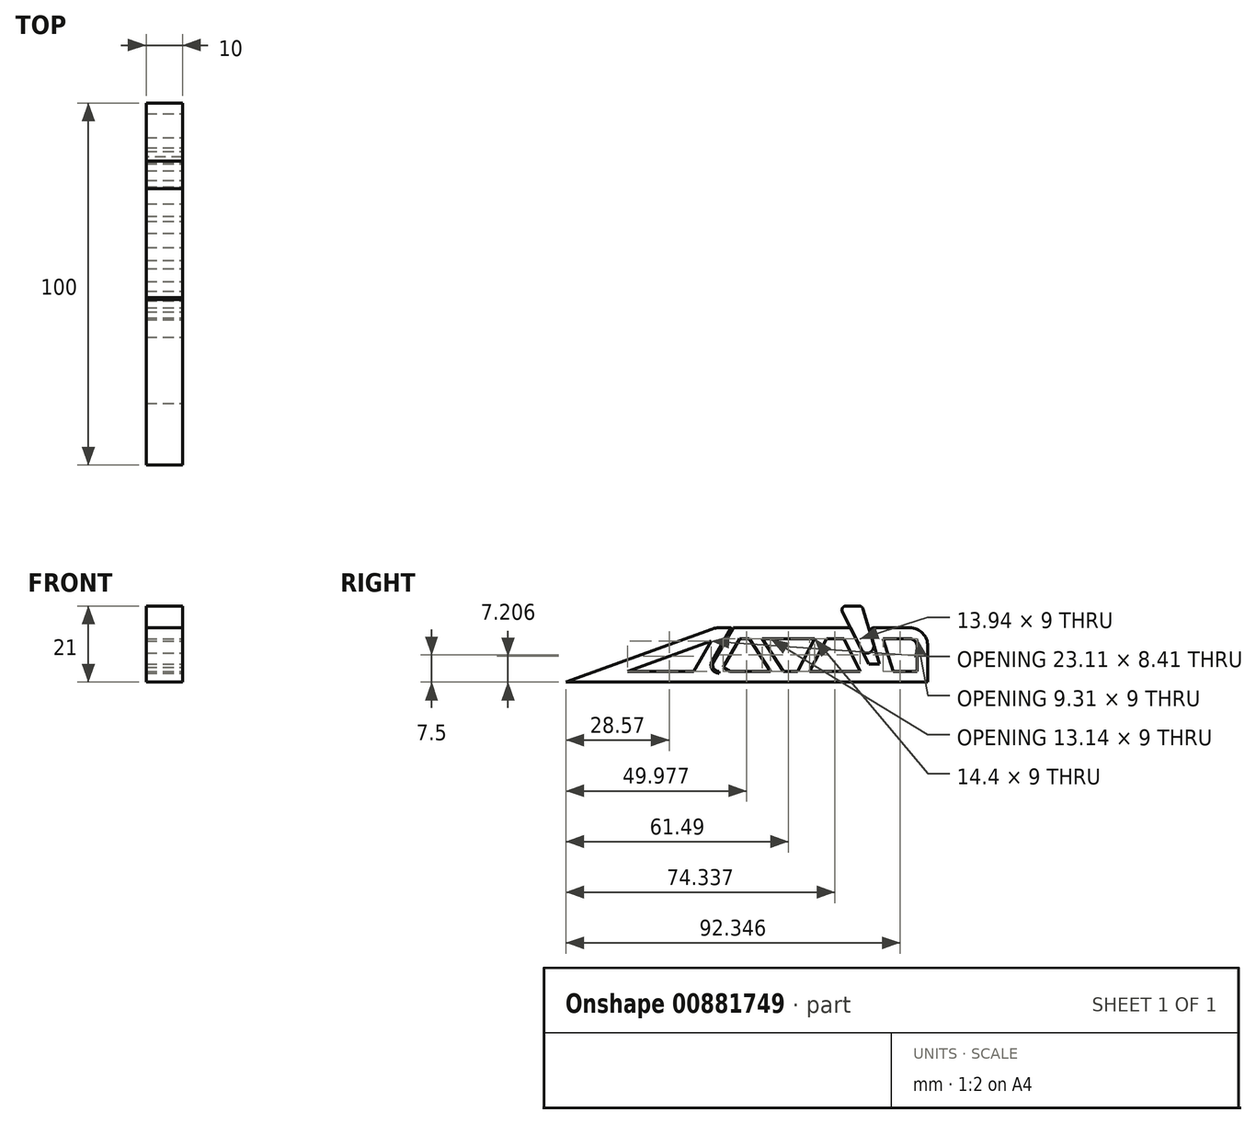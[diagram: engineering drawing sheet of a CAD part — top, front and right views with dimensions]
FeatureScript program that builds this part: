
annotation { "Feature Type Name" : "Feature", "Feature Type Description" : "" }
export const myFeature = defineFeature(function(context is Context, id is Id, definition is map)
    precondition{}
    {
        {
            var Q0;
            Q0=qCreatedBy(makeId("Right.planeOp"),FACE);
            var sketch = newSketch(context, id + "F0", { "sketchPlane" : qUnion([Q0])});
            skLineSegment(sketch, "E0", {"start": v(-50, 0) * mm, "end": v(50, 0) * mm});
            skLineSegment(sketch, "E1", {"start": v(-50, 0) * mm, "end": v(-8.79, 15) * mm});
            skLineSegment(sketch, "E2", {"start": v(50, 0) * mm, "end": v(50, 15) * mm});
            skLineSegment(sketch, "E3", {"start": v(-8.79, 15) * mm, "end": v(50, 15) * mm});
            skSolve(sketch);
        }
        {
            var Q0;
            Q0=qSketchRegion(id+"F0",true);
            extrude(context, id + "F1", {"entities" : qUnion([Q0]), "endBound" : BoundingType.SYMMETRIC, "depth" : 10 * mm, "offsetDistance" : 25 * mm});
        }
        {
            var Q0;
            Q0=makeQuery(id+"F1.opExtrude","SWEPT_EDGE",EDGE,{"disambiguationData":[OSD([sQuery(id+"F0.wireOp",EDGE,"E2"),sQuery(id+"F0.wireOp",EDGE,"E3")])]});
            var Q1;
            Q1=makeQuery(id+"F1.opExtrude","SWEPT_EDGE",EDGE,{"disambiguationData":[OSD([sQuery(id+"F0.wireOp",EDGE,"E1"),sQuery(id+"F0.wireOp",EDGE,"E3")])]});
            var Q2;
            Q2=makeQuery(id+"FClCLpVwUMpyTBV_1.opFillet","BLEND_EDGE",EDGE,{"blendedFrom":[makeQuery(id+"F1.opExtrude","SWEPT_EDGE",EDGE,{"disambiguationData":[OSD([sQuery(id+"F0.wireOp",EDGE,"E0"),sQuery(id+"F0.wireOp",EDGE,"E2")])]}),makeQuery(id+"F1.opExtrude","SWEPT_FACE",FACE,{"disambiguationData":[OSD([sQuery(id+"F0.wireOp",EDGE,"E3")])]})],"blendedInto":[makeQuery(id+"F1.opExtrude","SWEPT_FACE",FACE,{"disambiguationData":[OSD([sQuery(id+"F0.wireOp",EDGE,"E3")])]})]});
            fillet(context, id + "F2", {"entities" : qUnion([Q0, Q1, Q2]), "radius" : 5 * mm, "tangentPropagation" : true, "allowEdgeOverflow" : false});
        }
        {
            var Q0;
            Q0=makeQuery(id+"F1.opExtrude","CAP_FACE",FACE,{"disambiguationData":[OSD([sQuery(id+"F0.wireOp",EDGE,"E0"),sQuery(id+"F0.wireOp",EDGE,"E1"),sQuery(id+"F0.wireOp",EDGE,"E2"),sQuery(id+"F0.wireOp",EDGE,"E3")])],"isStart":false});
            var sketch = newSketch(context, id + "F3", { "sketchPlane" : qUnion([Q0])});
            skLineSegment(sketch, "E4", {"start": v(-4.34, 15) * mm, "end": v(-9.62, 5.85) * mm});
            skArc(sketch, "E5", {"start": v(-9.62, 5.85) * mm, "mid": v(-9.62, 3.61) * mm, "end": v(-7.68, 2.5) * mm});
            skLineSegment(sketch, "E6.0", {"start": v(-3.76, 15) * mm, "end": v(-9.2, 5.6) * mm});
            skArc(sketch, "E7.0", {"start": v(-9.2, 5.6) * mm, "mid": v(-9.19, 3.86) * mm, "end": v(-7.68, 3) * mm});
            skLineSegment(sketch, "E8", {"start": v(-4.34, 15) * mm, "end": v(-3.76, 15) * mm});
            skLineSegment(sketch, "E9", {"start": v(-7.68, 3) * mm, "end": v(-7.68, 2.5) * mm});
            skLineSegment(sketch, "E10", {"start": v(28.66, 15) * mm, "end": v(33.66, 5) * mm});
            skLineSegment(sketch, "E11", {"start": v(33.66, 15) * mm, "end": v(36.66, 5) * mm});
            skLineSegment(sketch, "E12", {"start": v(33.66, 5) * mm, "end": v(36.66, 5) * mm});
            skPoint(sketch, "E13.visualSharp", {"position": v(33.66, 5) * mm});
            skLineSegment(sketch, "E14", {"start": v(28.66, 15) * mm, "end": v(33.66, 15) * mm});
            skSolve(sketch);
        }
        {
            var Q0;
            Q0=qSketchRegion(id+"F3",true);
            extrude(context, id + "F4", {"entities" : qUnion([Q0]), "operationType" : NewBodyOperationType.REMOVE, "oppositeDirection" : true, "depth" : 25 * mm, "offsetDistance" : 25 * mm});
        }
        {
            var Q0;
            Q0=makeQuery(id+"F1.opExtrude","CAP_FACE",FACE,{"disambiguationData":[OSD([sQuery(id+"F0.wireOp",EDGE,"E0"),sQuery(id+"F0.wireOp",EDGE,"E1"),sQuery(id+"F0.wireOp",EDGE,"E2"),sQuery(id+"F0.wireOp",EDGE,"E3")])],"isStart":false});
            var sketch = newSketch(context, id + "F5", { "sketchPlane" : qUnion([Q0])});
            skLineSegment(sketch, "E15", {"start": v(32.16, 8) * mm, "end": v(25.66, 21) * mm});
            skLineSegment(sketch, "E16", {"start": v(35.76, 8) * mm, "end": v(31.86, 21) * mm});
            skLineSegment(sketch, "E17.0", {"start": v(32.16, 8) * mm, "end": v(35.76, 8) * mm});
            skLineSegment(sketch, "E18.0", {"start": v(25.66, 21) * mm, "end": v(31.86, 21) * mm});
            skSolve(sketch);
        }
        {
            var Q0;
            Q0=qSketchRegion(id+"F5",true);
            extrude(context, id + "F6", {"entities" : qUnion([Q0]), "oppositeDirection" : true, "depth" : 10 * mm, "offsetDistance" : 25 * mm});
        }
        {
            var Q0;
            Q0=makeQuery(id+"F1.opExtrude","CAP_FACE",FACE,{"disambiguationData":[OSD([sQuery(id+"F0.wireOp",EDGE,"E0"),sQuery(id+"F0.wireOp",EDGE,"E1"),sQuery(id+"F0.wireOp",EDGE,"E2"),sQuery(id+"F0.wireOp",EDGE,"E3")])],"isStart":false});
            var sketch = newSketch(context, id + "F7", { "sketchPlane" : qUnion([Q0])});
            skLineSegment(sketch, "E19.0", {"start": v(-48.97, -2.82) * mm, "end": v(-8.6, 11.88) * mm});
            skLineSegment(sketch, "E20.0", {"start": v(-50, 3) * mm, "end": v(31.3, 3) * mm});
            skLineSegment(sketch, "E21.0", {"start": v(-6.93, 16.5) * mm, "end": v(-14.73, 3) * mm});
            skLineSegment(sketch, "E22.0", {"start": v(-1.22, 13.4) * mm, "end": v(-6.6, 4.1) * mm});
            skLineSegment(sketch, "E23", {"start": v(-6.6, 4.1) * mm, "end": v(-3.47, 2.3) * mm});
            skLineSegment(sketch, "E24.0", {"start": v(-3.98, 12) * mm, "end": v(0.72, 12) * mm});
            skLineSegment(sketch, "E25.0", {"start": v(26.8, 12) * mm, "end": v(31.3, 3) * mm});
            skLineSegment(sketch, "E26.0", {"start": v(37.7, 12) * mm, "end": v(40.4, 3) * mm});
            skLineSegment(sketch, "E27.0", {"start": v(37.7, 12) * mm, "end": v(45, 12) * mm});
            skLineSegment(sketch, "E28", {"start": v(1.09, 14.19) * mm, "end": v(8.33, 3) * mm});
            skLineSegment(sketch, "E29", {"start": v(20.38, 12) * mm, "end": v(15.68, 3) * mm});
            skLineSegment(sketch, "E30.0", {"start": v(0.72, 12) * mm, "end": v(7.07, 2.18) * mm});
            skLineSegment(sketch, "E31.0", {"start": v(3.76, 12.82) * mm, "end": v(10.12, 3) * mm});
            skLineSegment(sketch, "E32.0", {"start": v(19.05, 12.7) * mm, "end": v(13.98, 3) * mm});
            skLineSegment(sketch, "E33.0", {"start": v(22.08, 12) * mm, "end": v(17, 2.3) * mm});
            skLineSegment(sketch, "E34.trimOffspring", {"start": v(4.29, 12) * mm, "end": v(18.7, 12) * mm});
            skLineSegment(sketch, "E35.trimOffspring", {"start": v(22.08, 12) * mm, "end": v(26.8, 12) * mm});
            skLineSegment(sketch, "E36.0", {"start": v(-50, -3) * mm, "end": v(50, -3) * mm});
            skLineSegment(sketch, "E37", {"start": v(38.2, 3) * mm, "end": v(51.36, 3) * mm});
            skLineSegment(sketch, "E38.0", {"start": v(47, 0) * mm, "end": v(47, 10) * mm});
            skArc(sketch, "E39.0", {"start": v(47, 10) * mm, "mid": v(46.41, 11.41) * mm, "end": v(45, 12) * mm});
            skSolve(sketch);
        }
        {
            var Q0;
            Q0=qSketchRegion(id+"F7",true);
            extrude(context, id + "F8", {"entities" : qUnion([Q0]), "operationType" : NewBodyOperationType.REMOVE, "oppositeDirection" : true, "depth" : 25 * mm, "offsetDistance" : 25 * mm});
        }
        {
            var Q0;
            Q0=makeQuery(id+"F4.boolean.opBoolean","COPY",EDGE,{"derivedFrom":makeQuery(id+"F4.opExtrude","SWEPT_EDGE",EDGE,{"disambiguationData":[OSD([sQuery(id+"F0.wireOp",EDGE,"E3"),sQuery(id+"F3.wireOp",EDGE,"E4"),sQuery(id+"F3.wireOp",EDGE,"E8")])]})});
            var Q1;
            Q1=makeQuery(id+"F4.boolean.opBoolean","COPY",EDGE,{"derivedFrom":makeQuery(id+"F4.opExtrude","SWEPT_EDGE",EDGE,{"disambiguationData":[OSD([sQuery(id+"F0.wireOp",EDGE,"E3"),sQuery(id+"F3.wireOp",EDGE,"E11"),sQuery(id+"F3.wireOp",EDGE,"E14")])]})});
            fillet(context, id + "F9", {"entities" : qUnion([Q0, Q1]), "radius" : 1 * mm, "tangentPropagation" : true, "allowEdgeOverflow" : false});
        }
        {
            var Q0;
            Q0=makeQuery(id+"F6.opExtrude","SWEPT_EDGE",EDGE,{"disambiguationData":[OSD([sQuery(id+"F3.wireOp",EDGE,"E10"),sQuery(id+"F5.wireOp",EDGE,"E15"),sQuery(id+"F5.wireOp",EDGE,"E17.0")])]});
            var Q1;
            Q1=makeQuery(id+"F6.opExtrude","SWEPT_EDGE",EDGE,{"disambiguationData":[OSD([sQuery(id+"F3.wireOp",EDGE,"E11"),sQuery(id+"F5.wireOp",EDGE,"E16"),sQuery(id+"F5.wireOp",EDGE,"E17.0")])]});
            fillet(context, id + "F10", {"entities" : qUnion([Q0, Q1]), "radius" : 2 * mm, "tangentPropagation" : true, "allowEdgeOverflow" : false});
        }
        {
            var Q0;
            Q0=makeQuery(id+"F6.opExtrude","SWEPT_EDGE",EDGE,{"disambiguationData":[OSD([sQuery(id+"F5.wireOp",EDGE,"E15"),sQuery(id+"F5.wireOp",EDGE,"E18.0")])]});
            var Q1;
            Q1=makeQuery(id+"F6.opExtrude","SWEPT_EDGE",EDGE,{"disambiguationData":[OSD([sQuery(id+"F5.wireOp",EDGE,"E16"),sQuery(id+"F5.wireOp",EDGE,"E18.0")])]});
            fillet(context, id + "F11", {"entities" : qUnion([Q0, Q1]), "radius" : 1 * mm, "tangentPropagation" : true, "allowEdgeOverflow" : false});
        }
    });
